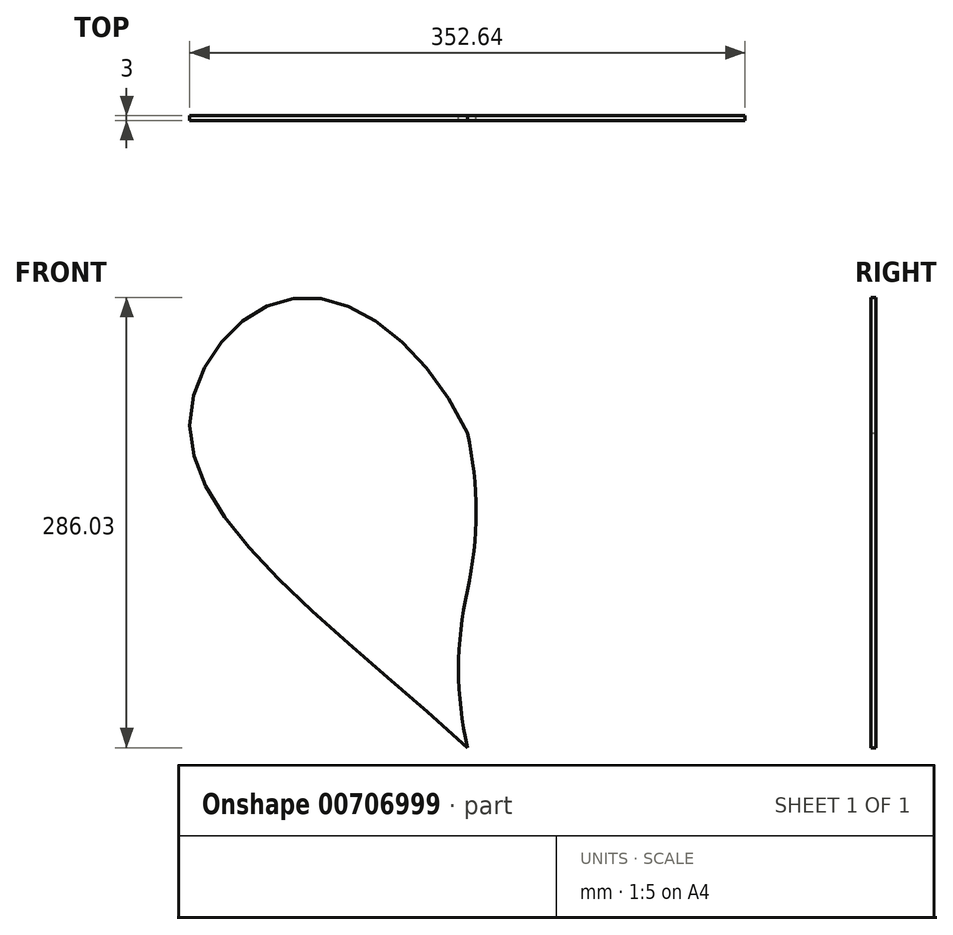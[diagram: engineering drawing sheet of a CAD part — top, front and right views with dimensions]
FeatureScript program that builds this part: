
annotation { "Feature Type Name" : "Feature", "Feature Type Description" : "" }
export const myFeature = defineFeature(function(context is Context, id is Id, definition is map)
    precondition{}
    {
        {
            var Q0;
            Q0=qCreatedBy(makeId("Front.planeOp"),FACE);
            var sketch = newSketch(context, id + "F0", { "sketchPlane" : qUnion([Q0])});
            skFitSpline(sketch, "E0", {"points": [v(0, 0) * mm, v(-176.16, 199.8) * mm, v(-111.86, 285.26) * mm, v(0, 200) * mm], "startDerivative": vector(-583.05, 534.32) * mm, "endDerivative": vector(252.94, -524.65) * mm});
            skFitSpline(sketch, "E1.MirrorCS", {"points": [v(0, 0) * mm, v(176.16, 199.8) * mm, v(111.86, 285.26) * mm, v(0, 200) * mm], "startDerivative": vector(583.05, 534.32) * mm, "endDerivative": vector(-252.94, -524.65) * mm});
            skLineSegment(sketch, "E2", {"start": v(0, 200) * mm, "end": v(0, 0) * mm});
            skArc(sketch, "E3", {"start": v(0, 100) * mm, "mid": v(5.56, 150) * mm, "end": v(0, 200) * mm});
            skArc(sketch, "E4", {"start": v(0, 100) * mm, "mid": v(-5.58, 50) * mm, "end": v(0, 0) * mm});
            skSolve(sketch);
        }
        {
            var Q0;
            {var subQ0=sQuery(id+"F0.wireOp",EDGE,"E1.MirrorCS");Q0=makeQuery(id+"F0.imprint","IMPRINT",FACE,{"disambiguationData":[TD([[makeQuery(id+"F0.imprint","IMPRINT",EDGE,{"derivedFrom":subQ0}),1.0]])]});}
            var Q1;
            {var subQ0=sQuery(id+"F0.wireOp",EDGE,"E4");Q1=makeQuery(id+"F0.imprint","IMPRINT",FACE,{"disambiguationData":[TD([[makeQuery(id+"F0.imprint","IMPRINT",EDGE,{"derivedFrom":subQ0}),1.0]])]});}
            extrude(context, id + "F1", {"entities" : qUnion([Q0, Q1]), "depth" : 3 * mm, "offsetDistance" : 25 * mm});
        }
        {
            var Q0;
            {var subQ0=sQuery(id+"F0.wireOp",EDGE,"pOiCyq85-TZA7-Dpjo-Xp75-GD3030ydBp2L");Q0=makeQuery(id+"F0.imprint","IMPRINT",FACE,{"disambiguationData":[TD([[makeQuery(id+"F0.imprint","IMPRINT",EDGE,{"derivedFrom":subQ0}),1.0]])]});}
            var Q1;
            {var subQ0=sQuery(id+"F0.wireOp",EDGE,"E3");Q1=makeQuery(id+"F0.imprint","IMPRINT",FACE,{"disambiguationData":[TD([[makeQuery(id+"F0.imprint","IMPRINT",EDGE,{"derivedFrom":subQ0}),1.0]])]});}
            var Q2;
            {var subQ0=sQuery(id+"F0.wireOp",EDGE,"E0");Q2=makeQuery(id+"F0.imprint","IMPRINT",FACE,{"disambiguationData":[TD([[makeQuery(id+"F0.imprint","IMPRINT",EDGE,{"derivedFrom":subQ0}),-1.0]])]});}
            extrude(context, id + "F2", {"entities" : qUnion([Q0, Q1, Q2]), "depth" : 3 * mm, "offsetDistance" : 25 * mm});
        }
    });
